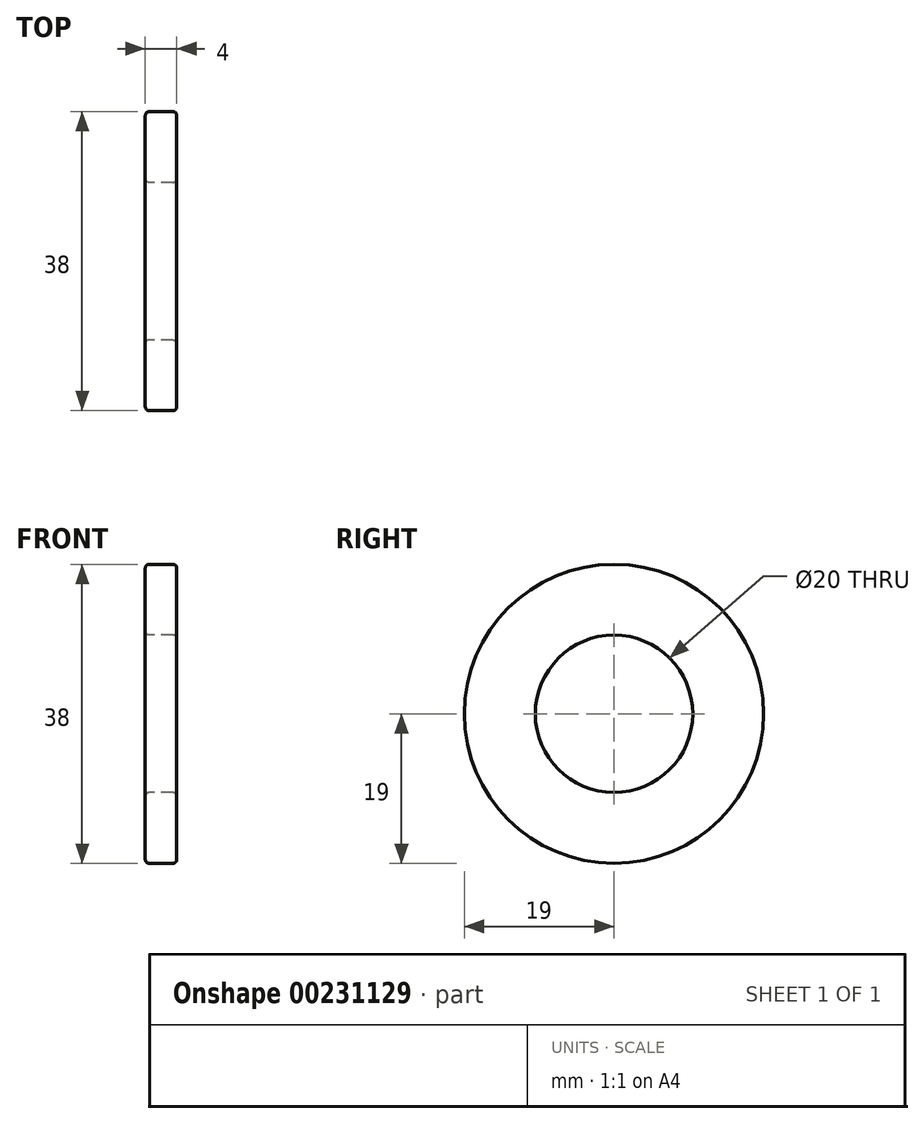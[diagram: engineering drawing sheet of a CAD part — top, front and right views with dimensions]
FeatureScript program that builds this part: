
annotation { "Feature Type Name" : "Feature", "Feature Type Description" : "" }
export const myFeature = defineFeature(function(context is Context, id is Id, definition is map)
    precondition{}
    {
        {
            var Q0;
            Q0=qCreatedBy(makeId("Right.planeOp"),FACE);
            var sketch = newSketch(context, id + "F0", { "sketchPlane" : qUnion([Q0])});
            skCircle(sketch, "E0", {"center": v(0, 0) * mm, "radius": 19 * mm});
            skCircle(sketch, "E1", {"center": v(0, 0) * mm, "radius": 10 * mm});
            skSolve(sketch);
        }
        {
            var Q0;
            Q0=makeQuery(id+"F0.imprint","IMPRINT",FACE,{"disambiguationData":[TD([[makeQuery(id+"F0.imprint","IMPRINT",EDGE,{"derivedFrom":sQuery(id+"F0.wireOp",EDGE,"E0")}),1.0]])]});
            extrude(context, id + "F1", {"entities" : qUnion([Q0]), "endBound" : BoundingType.SYMMETRIC, "depth" : 4 * mm});
        }
        {
            var Q0;
            Q0=makeQuery(id+"F1.opExtrude","CAP_EDGE",EDGE,{"disambiguationData":[OSD([sQuery(id+"F0.wireOp",EDGE,"E1")])],"isStart":false});
            var Q1;
            Q1=makeQuery(id+"F1.opExtrude","CAP_EDGE",EDGE,{"disambiguationData":[OSD([sQuery(id+"F0.wireOp",EDGE,"E1")])],"isStart":true});
            var Q2;
            Q2=makeQuery(id+"F1.opExtrude","CAP_FACE",FACE,{"disambiguationData":[OSD([sQuery(id+"F0.wireOp",EDGE,"E0"),sQuery(id+"F0.wireOp",EDGE,"E1")])],"isStart":false});
            var Q3;
            Q3=makeQuery(id+"F1.opExtrude","CAP_EDGE",EDGE,{"disambiguationData":[OSD([sQuery(id+"F0.wireOp",EDGE,"E0")])],"isStart":true});
            fillet(context, id + "F2", {"entities" : qUnion([Q0, Q1, Q2, Q3]), "radius" : 0.5 * mm, "tangentPropagation" : true, "allowEdgeOverflow" : false});
        }
    });
